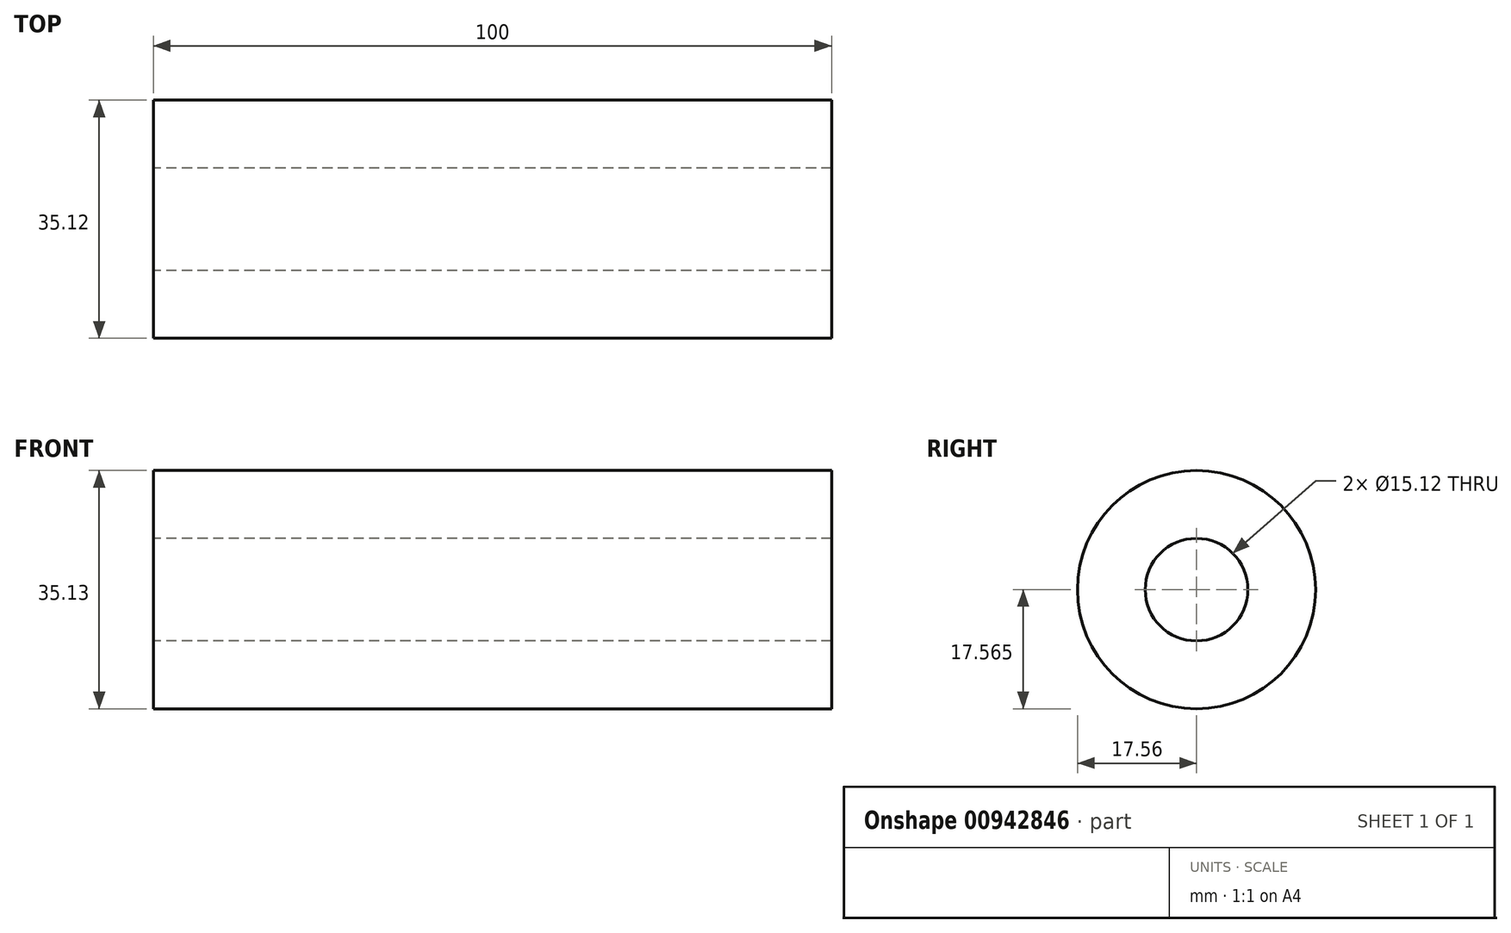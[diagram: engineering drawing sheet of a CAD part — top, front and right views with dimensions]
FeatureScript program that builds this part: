
annotation { "Feature Type Name" : "Feature", "Feature Type Description" : "" }
export const myFeature = defineFeature(function(context is Context, id is Id, definition is map)
    precondition{}
    {
        {
            var Q0;
            Q0=qCreatedBy(makeId("Front.planeOp"),FACE);
            var sketch = newSketch(context, id + "F0", { "sketchPlane" : qUnion([Q0])});
            skLineSegment(sketch, "E0", {"start": v(-39.73, 33.17) * mm, "end": v(60.27, 33.17) * mm});
            skLineSegment(sketch, "E1", {"start": v(-39.73, 33.17) * mm, "end": v(-39.73, 23.17) * mm});
            skLineSegment(sketch, "E2", {"start": v(-39.73, 23.17) * mm, "end": v(60.27, 23.17) * mm});
            skLineSegment(sketch, "E3", {"start": v(60.27, 23.17) * mm, "end": v(60.27, 33.17) * mm});
            skSolve(sketch);
        }
        {
            var Q0;
            Q0=makeQuery(id+"F0.imprint","IMPRINT",FACE,{"disambiguationData":[TD([[makeQuery(id+"F0.imprint","IMPRINT",EDGE,{"derivedFrom":sQuery(id+"F0.wireOp",EDGE,"E0")}),-1.0]])]});
            var sketch = newSketch(context, id + "F1", { "sketchPlane" : qUnion([Q0])});
            skLineSegment(sketch, "E4", {"start": v(-39.81, 25.6) * mm, "end": v(-39.81, 15.6) * mm, "construction": true});
            skLineSegment(sketch, "E5", {"start": v(-39.81, 15.6) * mm, "end": v(59.97, 15.6) * mm, "construction": true});
            skLineSegment(sketch, "E6", {"start": v(59.97, 15.6) * mm, "end": v(59.97, 25.6) * mm, "construction": true});
            skSolve(sketch);
        }
        {
            var Q0;
            Q0=makeQuery(id+"F0.imprint","IMPRINT",FACE,{"disambiguationData":[TD([[makeQuery(id+"F0.imprint","IMPRINT",EDGE,{"derivedFrom":sQuery(id+"F0.wireOp",EDGE,"E0")}),-1.0]])]});
            var Q1;
            Q1=sQuery(id+"F1.wireOp",EDGE,"E5");
            revolve(context, id + "F2", {"surfaceOperationType" : NewSurfaceOperationType.NEW, "entities" : qUnion([Q0]), "axis" : qUnion([Q1]), "revolveType" : RevolveType.FULL});
        }
    });
